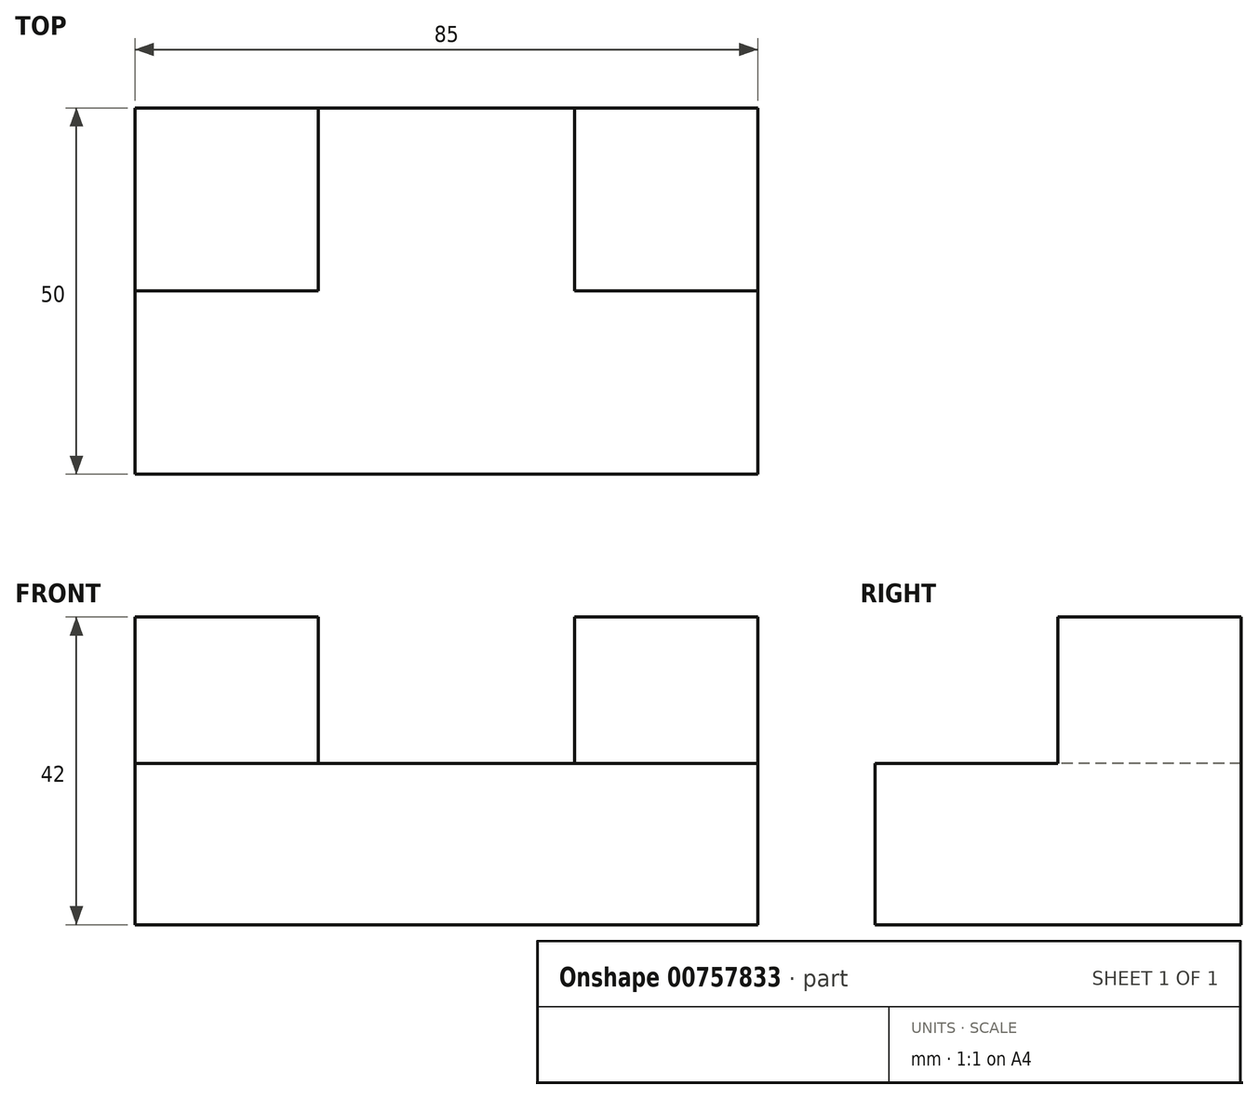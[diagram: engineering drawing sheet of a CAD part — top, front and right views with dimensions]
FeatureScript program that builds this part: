
annotation { "Feature Type Name" : "Feature", "Feature Type Description" : "" }
export const myFeature = defineFeature(function(context is Context, id is Id, definition is map)
    precondition{}
    {
        {
            var Q0;
            Q0=qCreatedBy(makeId("Front.planeOp"),FACE);
            var sketch = newSketch(context, id + "F0", { "sketchPlane" : qUnion([Q0])});
            skLineSegment(sketch, "E0.bottom", {"start": v(0, 0) * mm, "end": v(85, 0) * mm});
            skLineSegment(sketch, "E0.top", {"start": v(0, 42) * mm, "end": v(85, 42) * mm});
            skLineSegment(sketch, "E0.left", {"start": v(0, 0) * mm, "end": v(0, 42) * mm});
            skLineSegment(sketch, "E0.right", {"start": v(85, 0) * mm, "end": v(85, 42) * mm});
            skSolve(sketch);
        }
        {
            var Q0;
            Q0 = qSketchRegion(id + "F0", true);
            extrude(context, id + "F1", {"entities" : qUnion([Q0]), "depth" : 50 * mm, "offsetDistance" : 25 * mm});
        }
        {
            var Q0;
            Q0=makeQuery(id+"F1.opExtrude","CAP_FACE",FACE,{"disambiguationData":[OSD([sQuery(id+"F0.wireOp",EDGE,"E0.bottom"),sQuery(id+"F0.wireOp",EDGE,"E0.top"),sQuery(id+"F0.wireOp",EDGE,"E0.left"),sQuery(id+"F0.wireOp",EDGE,"E0.right")])],"isStart":false});
            var sketch = newSketch(context, id + "F2", { "sketchPlane" : qUnion([Q0])});
            skLineSegment(sketch, "E1.bottom", {"start": v(0, 42) * mm, "end": v(25, 42) * mm});
            skLineSegment(sketch, "E1.top", {"start": v(0, 22) * mm, "end": v(25, 22) * mm});
            skLineSegment(sketch, "E1.left", {"start": v(0, 42) * mm, "end": v(0, 22) * mm});
            skLineSegment(sketch, "E1.right", {"start": v(25, 42) * mm, "end": v(25, 22) * mm});
            skLineSegment(sketch, "E2.bottom", {"start": v(85, 42) * mm, "end": v(60, 42) * mm});
            skLineSegment(sketch, "E2.top", {"start": v(85, 22) * mm, "end": v(60, 22) * mm});
            skLineSegment(sketch, "E2.left", {"start": v(85, 42) * mm, "end": v(85, 22) * mm});
            skLineSegment(sketch, "E2.right", {"start": v(60, 42) * mm, "end": v(60, 22) * mm});
            skSolve(sketch);
        }
        {
            var Q0;
            Q0 = qSketchRegion(id + "F2", true);
            extrude(context, id + "F3", {"entities" : qUnion([Q0]), "operationType" : NewBodyOperationType.REMOVE, "oppositeDirection" : true, "depth" : 25 * mm, "offsetDistance" : 25 * mm});
        }
        {
            var Q0;
            Q0=makeQuery(id+"F1.opExtrude","CAP_FACE",FACE,{"disambiguationData":[OSD([sQuery(id+"F0.wireOp",EDGE,"E0.bottom"),sQuery(id+"F0.wireOp",EDGE,"E0.top"),sQuery(id+"F0.wireOp",EDGE,"E0.left"),sQuery(id+"F0.wireOp",EDGE,"E0.right")])],"isStart":false});
            var sketch = newSketch(context, id + "F4", { "sketchPlane" : qUnion([Q0])});
            skLineSegment(sketch, "E3.bottom", {"start": v(25, 42) * mm, "end": v(60, 42) * mm});
            skLineSegment(sketch, "E3.top", {"start": v(25, 22) * mm, "end": v(60, 22) * mm});
            skLineSegment(sketch, "E3.left", {"start": v(25, 42) * mm, "end": v(25, 22) * mm});
            skLineSegment(sketch, "E3.right", {"start": v(60, 42) * mm, "end": v(60, 22) * mm});
            skSolve(sketch);
        }
        {
            var Q0;
            Q0 = qSketchRegion(id + "F4", true);
            extrude(context, id + "F5", {"entities" : qUnion([Q0]), "operationType" : NewBodyOperationType.REMOVE, "endBound" : BoundingType.THROUGH_ALL, "oppositeDirection" : true, "depth" : 25 * mm, "offsetDistance" : 25 * mm});
        }
    });
